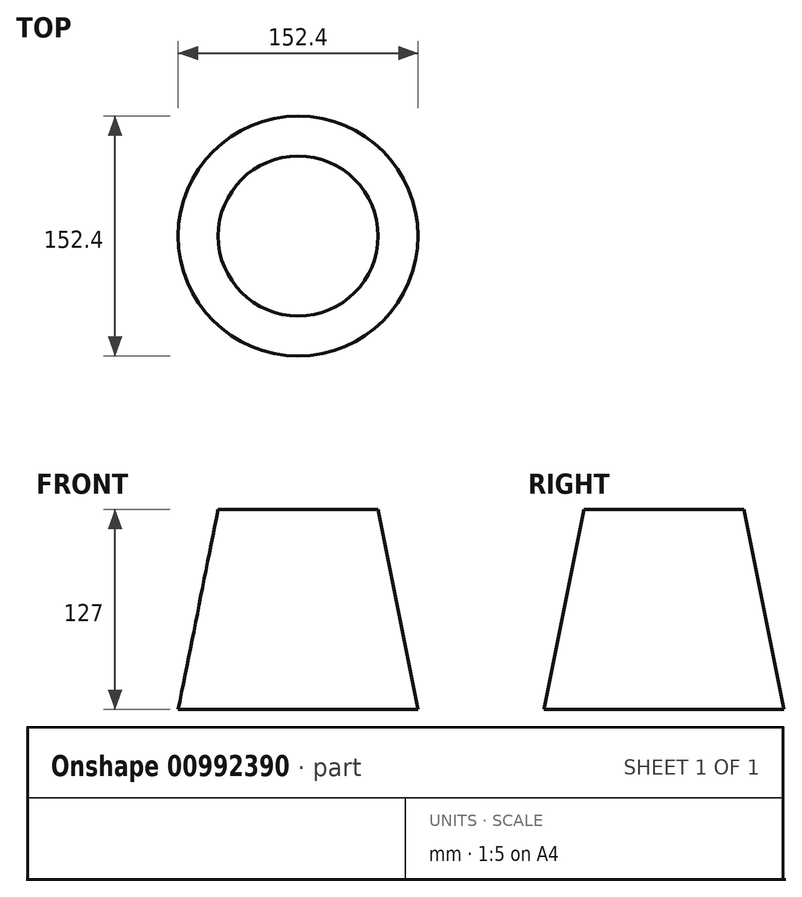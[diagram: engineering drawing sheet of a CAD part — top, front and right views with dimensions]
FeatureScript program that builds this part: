
annotation { "Feature Type Name" : "Feature", "Feature Type Description" : "" }
export const myFeature = defineFeature(function(context is Context, id is Id, definition is map)
    precondition{}
    {
        {
            var Q0;
            Q0=qCreatedBy(makeId("Front.planeOp"),FACE);
            var sketch = newSketch(context, id + "F0", { "sketchPlane" : qUnion([Q0])});
            skLineSegment(sketch, "E0", {"start": v(0, 0) * mm, "end": v(0, 63.5) * mm});
            skLineSegment(sketch, "E1", {"start": v(0, 0) * mm, "end": v(0, -63.5) * mm});
            skLineSegment(sketch, "E2", {"start": v(0, 63.5) * mm, "end": v(-50.8, 63.5) * mm});
            skLineSegment(sketch, "E3", {"start": v(0, -63.5) * mm, "end": v(-76.2, -63.5) * mm});
            skLineSegment(sketch, "E4", {"start": v(-76.2, -63.5) * mm, "end": v(-50.8, 63.5) * mm});
            skSolve(sketch);
        }
        {
            var Q0;
            Q0 = qSketchRegion(id + "F0", true);
            var Q1;
            Q1=sQuery(id+"F0.wireOp",EDGE,"E0");
            revolve(context, id + "F1", {"surfaceOperationType" : NewSurfaceOperationType.NEW, "entities" : qUnion([Q0]), "axis" : qUnion([Q1]), "revolveType" : RevolveType.FULL});
        }
    });
